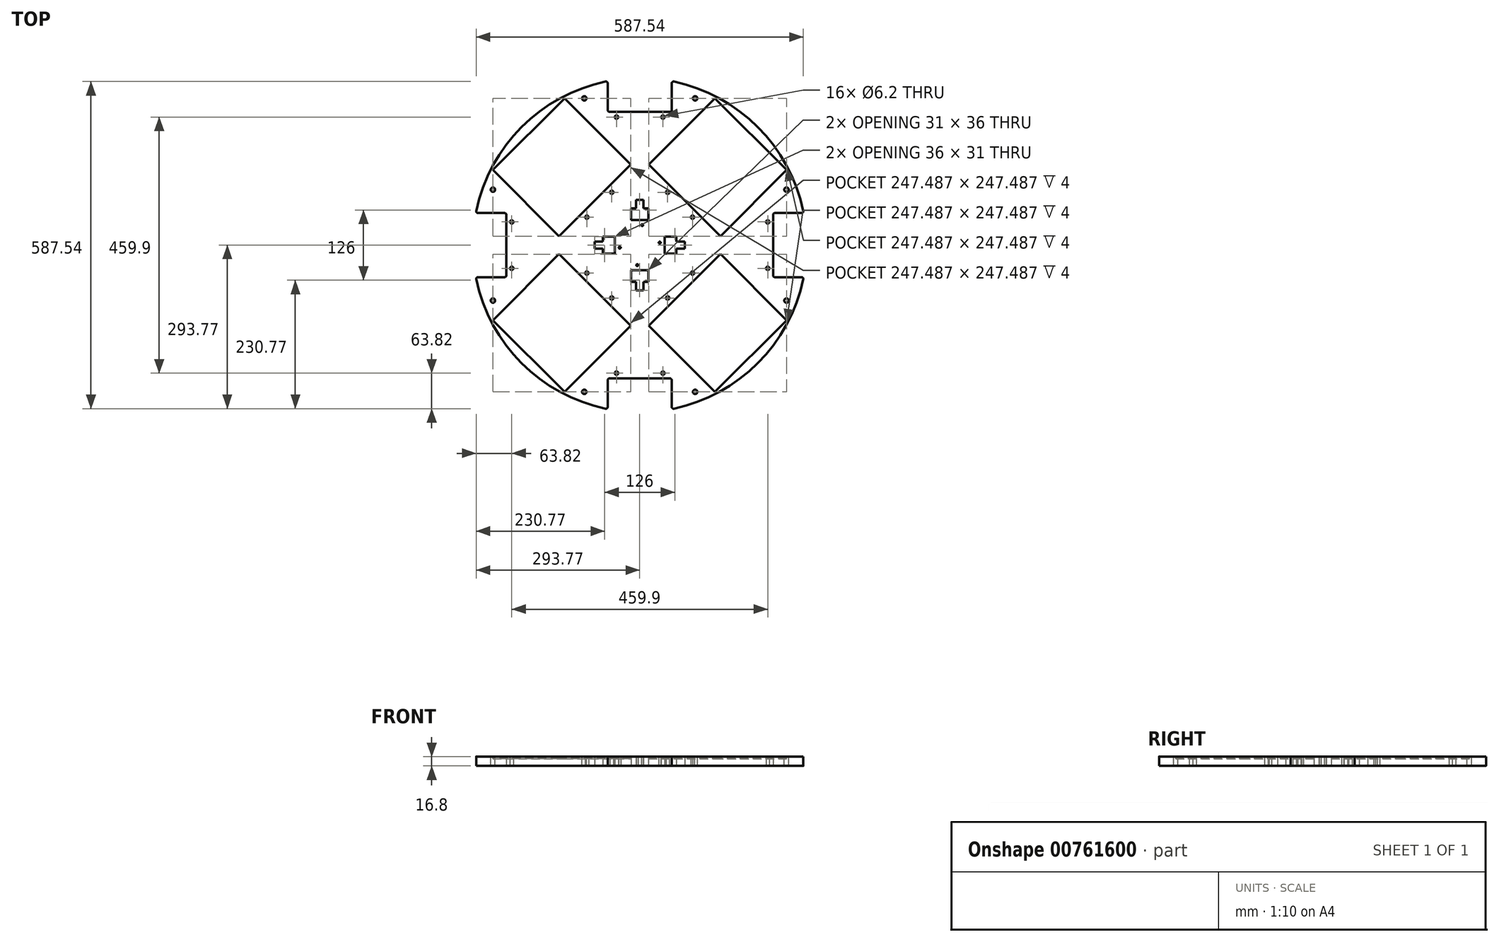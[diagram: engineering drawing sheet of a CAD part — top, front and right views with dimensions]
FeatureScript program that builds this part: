
annotation { "Feature Type Name" : "Feature", "Feature Type Description" : "" }
export const myFeature = defineFeature(function(context is Context, id is Id, definition is map)
    precondition{}
    {
        {
            var Q0;
            Q0=qCreatedBy(makeId("Top.planeOp"),FACE);
            var sketch = newSketch(context, id + "F0", { "sketchPlane" : qUnion([Q0])});
            skCircle(sketch, "E0", {"center": v(0, 0) * mm, "radius": 300 * mm});
            skLineSegment(sketch, "E1", {"start": v(300, 0) * mm, "end": v(-300, 0) * mm, "construction": true});
            skLineSegment(sketch, "E2", {"start": v(0, -300) * mm, "end": v(0, 300) * mm, "construction": true});
            skLineSegment(sketch, "E3.bottom", {"start": v(-296.52, 57.5) * mm, "end": v(-239.5, 57.5) * mm});
            skLineSegment(sketch, "E3.top", {"start": v(-296.52, -57.5) * mm, "end": v(-239.5, -57.5) * mm});
            skLineSegment(sketch, "E3.left", {"start": v(-296.52, 57.5) * mm, "end": v(-296.52, -57.5) * mm, "construction": true});
            skLineSegment(sketch, "E3.right", {"start": v(-239.5, 57.5) * mm, "end": v(-239.5, -57.5) * mm});
            skPoint(sketch, "E3.middle", {"position": v(-268, 0) * mm});
            skLineSegment(sketch, "E4.1.0", {"start": v(-57.5, -296.52) * mm, "end": v(-57.5, -239.5) * mm});
            skLineSegment(sketch, "E4.1.1", {"start": v(57.5, -296.52) * mm, "end": v(57.5, -239.5) * mm});
            skLineSegment(sketch, "E4.1.2", {"start": v(-57.5, -296.52) * mm, "end": v(57.5, -296.52) * mm});
            skLineSegment(sketch, "E4.1.3", {"start": v(-57.5, -239.5) * mm, "end": v(57.5, -239.5) * mm});
            skPoint(sketch, "E4.1.4", {"position": v(0, -268) * mm});
            skLineSegment(sketch, "E4.2.0", {"start": v(296.52, -57.5) * mm, "end": v(239.5, -57.5) * mm});
            skLineSegment(sketch, "E4.2.1", {"start": v(296.52, 57.5) * mm, "end": v(239.5, 57.5) * mm});
            skLineSegment(sketch, "E4.2.2", {"start": v(296.52, -57.5) * mm, "end": v(296.52, 57.5) * mm});
            skLineSegment(sketch, "E4.2.3", {"start": v(239.5, -57.5) * mm, "end": v(239.5, 57.5) * mm});
            skPoint(sketch, "E4.2.4", {"position": v(268, 0) * mm});
            skLineSegment(sketch, "E4.3.0", {"start": v(57.5, 296.52) * mm, "end": v(57.5, 239.5) * mm});
            skLineSegment(sketch, "E4.3.1", {"start": v(-57.5, 296.52) * mm, "end": v(-57.5, 239.5) * mm});
            skLineSegment(sketch, "E4.3.2", {"start": v(57.5, 296.52) * mm, "end": v(-57.5, 296.52) * mm});
            skLineSegment(sketch, "E4.3.3", {"start": v(57.5, 239.5) * mm, "end": v(-57.5, 239.5) * mm});
            skPoint(sketch, "E4.3.4", {"position": v(0, 268) * mm});
            skLineSegment(sketch, "E5", {"start": v(-239.5, -57.5) * mm, "end": v(-94.95, -57.5) * mm, "construction": true});
            skLineSegment(sketch, "E6", {"start": v(-229.95, -41.7) * mm, "end": v(-229.95, 0) * mm, "construction": true});
            skCircle(sketch, "E7", {"center": v(-229.95, -41.7) * mm, "radius": 3.1 * mm});
            skCircle(sketch, "E8.MirrorC", {"center": v(-229.95, 41.7) * mm, "radius": 3.1 * mm});
            skCircle(sketch, "E9.1.0", {"center": v(41.7, -229.95) * mm, "radius": 3.1 * mm});
            skCircle(sketch, "E9.1.1", {"center": v(-41.7, -229.95) * mm, "radius": 3.1 * mm});
            skCircle(sketch, "E9.2.0", {"center": v(229.95, 41.7) * mm, "radius": 3.1 * mm});
            skCircle(sketch, "E9.2.1", {"center": v(229.95, -41.7) * mm, "radius": 3.1 * mm});
            skCircle(sketch, "E9.3.0", {"center": v(-41.7, 229.95) * mm, "radius": 3.1 * mm});
            skCircle(sketch, "E9.3.1", {"center": v(41.7, 229.95) * mm, "radius": 3.1 * mm});
            skLineSegment(sketch, "E10", {"start": v(-94.95, -57.5) * mm, "end": v(-94.95, -50.2) * mm, "construction": true});
            skLineSegment(sketch, "E11", {"start": v(-94.95, -50.2) * mm, "end": v(-239.5, -50.2) * mm, "construction": true});
            skCircle(sketch, "E12", {"center": v(-94.95, -50.2) * mm, "radius": 3.1 * mm});
            skCircle(sketch, "E13.MirrorC", {"center": v(-94.95, 50.2) * mm, "radius": 3.1 * mm});
            skCircle(sketch, "E14.1.0", {"center": v(50.2, -94.95) * mm, "radius": 3.1 * mm});
            skCircle(sketch, "E14.1.1", {"center": v(-50.2, -94.95) * mm, "radius": 3.1 * mm});
            skCircle(sketch, "E14.2.0", {"center": v(94.95, 50.2) * mm, "radius": 3.1 * mm});
            skCircle(sketch, "E14.2.1", {"center": v(94.95, -50.2) * mm, "radius": 3.1 * mm});
            skCircle(sketch, "E14.3.0", {"center": v(-50.2, 94.95) * mm, "radius": 3.1 * mm});
            skCircle(sketch, "E14.3.1", {"center": v(50.2, 94.95) * mm, "radius": 3.1 * mm});
            skLineSegment(sketch, "E15", {"start": v(-294.44, 57.5) * mm, "end": v(-296.52, 57.5) * mm, "construction": true});
            skLineSegment(sketch, "E16", {"start": v(-294.44, 57.5) * mm, "end": v(-294.44, -57.5) * mm, "construction": true});
            skLineSegment(sketch, "E17", {"start": v(-296.52, -57.5) * mm, "end": v(-294.44, -57.5) * mm, "construction": true});
            skLineSegment(sketch, "E18.bottom", {"start": v(-45, -15.5) * mm, "end": v(-66, -15.5) * mm});
            skLineSegment(sketch, "E18.top", {"start": v(-45, 15.5) * mm, "end": v(-66, 15.5) * mm});
            skLineSegment(sketch, "E18.left", {"start": v(-45, -15.5) * mm, "end": v(-45, 15.5) * mm});
            skLineSegment(sketch, "E18.right", {"start": v(-66, -15.5) * mm, "end": v(-66, -6.5) * mm});
            skPoint(sketch, "E18.middle", {"position": v(-55.5, 0) * mm});
            skLineSegment(sketch, "E19", {"start": v(0, 0) * mm, "end": v(-229.45, 229.45) * mm, "construction": true});
            skLineSegment(sketch, "E20.MirrorCS", {"start": v(0, 0) * mm, "end": v(-229.45, -229.45) * mm, "construction": true});
            skLineSegment(sketch, "E21.MirrorCS", {"start": v(0, 0) * mm, "end": v(229.45, -229.45) * mm, "construction": true});
            skLineSegment(sketch, "E22", {"start": v(-66, 6.5) * mm, "end": v(-81, 6.5) * mm});
            skLineSegment(sketch, "E23", {"start": v(-81, 6.5) * mm, "end": v(-81, -6.5) * mm});
            skLineSegment(sketch, "E24", {"start": v(-81, -6.5) * mm, "end": v(-66, -6.5) * mm});
            skPoint(sketch, "E25", {"position": v(-81, 0) * mm});
            skLineSegment(sketch, "E26", {"start": v(-66, 6.5) * mm, "end": v(-66, 15.5) * mm});
            skLineSegment(sketch, "E27", {"start": v(-66, -6.5) * mm, "end": v(-66, 6.5) * mm, "construction": true});
            skLineSegment(sketch, "E28.1.0", {"start": v(-15.5, -45) * mm, "end": v(-15.5, -66) * mm});
            skPoint(sketch, "E28.1.1", {"position": v(0, -81) * mm});
            skLineSegment(sketch, "E28.1.2", {"start": v(-6.5, -66) * mm, "end": v(-6.5, -81) * mm});
            skLineSegment(sketch, "E28.1.3", {"start": v(15.5, -45) * mm, "end": v(15.5, -66) * mm});
            skLineSegment(sketch, "E28.1.4", {"start": v(15.5, -66) * mm, "end": v(6.5, -66) * mm});
            skLineSegment(sketch, "E28.1.5", {"start": v(15.5, -45) * mm, "end": v(-15.5, -45) * mm});
            skLineSegment(sketch, "E28.1.6", {"start": v(6.5, -66) * mm, "end": v(-6.5, -66) * mm, "construction": true});
            skLineSegment(sketch, "E28.1.7", {"start": v(-6.5, -81) * mm, "end": v(6.5, -81) * mm});
            skLineSegment(sketch, "E28.1.8", {"start": v(-6.5, -66) * mm, "end": v(-15.5, -66) * mm});
            skLineSegment(sketch, "E28.1.9", {"start": v(6.5, -81) * mm, "end": v(6.5, -66) * mm});
            skLineSegment(sketch, "E28.2.0", {"start": v(45, -15.5) * mm, "end": v(66, -15.5) * mm});
            skPoint(sketch, "E28.2.1", {"position": v(81, 0) * mm});
            skLineSegment(sketch, "E28.2.2", {"start": v(66, -6.5) * mm, "end": v(81, -6.5) * mm});
            skLineSegment(sketch, "E28.2.3", {"start": v(45, 15.5) * mm, "end": v(66, 15.5) * mm});
            skLineSegment(sketch, "E28.2.4", {"start": v(66, 15.5) * mm, "end": v(66, 6.5) * mm});
            skLineSegment(sketch, "E28.2.5", {"start": v(45, 15.5) * mm, "end": v(45, -15.5) * mm});
            skLineSegment(sketch, "E28.2.6", {"start": v(66, 6.5) * mm, "end": v(66, -6.5) * mm, "construction": true});
            skLineSegment(sketch, "E28.2.7", {"start": v(81, -6.5) * mm, "end": v(81, 6.5) * mm});
            skLineSegment(sketch, "E28.2.8", {"start": v(66, -6.5) * mm, "end": v(66, -15.5) * mm});
            skLineSegment(sketch, "E28.2.9", {"start": v(81, 6.5) * mm, "end": v(66, 6.5) * mm});
            skLineSegment(sketch, "E28.3.0", {"start": v(15.5, 45) * mm, "end": v(15.5, 66) * mm});
            skPoint(sketch, "E28.3.1", {"position": v(0, 81) * mm});
            skLineSegment(sketch, "E28.3.2", {"start": v(6.5, 66) * mm, "end": v(6.5, 81) * mm});
            skLineSegment(sketch, "E28.3.3", {"start": v(-15.5, 45) * mm, "end": v(-15.5, 66) * mm});
            skLineSegment(sketch, "E28.3.4", {"start": v(-15.5, 66) * mm, "end": v(-6.5, 66) * mm});
            skLineSegment(sketch, "E28.3.5", {"start": v(-15.5, 45) * mm, "end": v(15.5, 45) * mm});
            skLineSegment(sketch, "E28.3.6", {"start": v(-6.5, 66) * mm, "end": v(6.5, 66) * mm, "construction": true});
            skLineSegment(sketch, "E28.3.7", {"start": v(6.5, 81) * mm, "end": v(-6.5, 81) * mm});
            skLineSegment(sketch, "E28.3.8", {"start": v(6.5, 66) * mm, "end": v(15.5, 66) * mm});
            skLineSegment(sketch, "E28.3.9", {"start": v(-6.5, 81) * mm, "end": v(-6.5, 66) * mm});
            skLineSegment(sketch, "E29", {"start": v(-23.74, -23.74) * mm, "end": v(-46.55, -0.94) * mm, "construction": true});
            skLineSegment(sketch, "E30", {"start": v(-23.74, -23.74) * mm, "end": v(-0.94, -46.55) * mm, "construction": true});
            skLineSegment(sketch, "E31.MirrorCS", {"start": v(23.74, 23.74) * mm, "end": v(0.94, 46.55) * mm, "construction": true});
            skLineSegment(sketch, "E32.MirrorCS", {"start": v(23.74, 23.74) * mm, "end": v(46.55, 0.94) * mm, "construction": true});
            skLineSegment(sketch, "E33", {"start": v(-46.55, -0.94) * mm, "end": v(0.94, 46.55) * mm, "construction": true});
            skLineSegment(sketch, "E34", {"start": v(-0.94, -46.55) * mm, "end": v(46.55, 0.94) * mm, "construction": true});
            skCircle(sketch, "E35", {"center": v(4.47, 35.94) * mm, "radius": 1.75 * mm});
            skCircle(sketch, "E36.MirrorC", {"center": v(35.94, 4.47) * mm, "radius": 1.75 * mm});
            skCircle(sketch, "E37.MirrorC", {"center": v(-35.94, -4.47) * mm, "radius": 1.75 * mm});
            skCircle(sketch, "E38.MirrorC", {"center": v(-4.47, -35.94) * mm, "radius": 1.75 * mm});
            skLineSegment(sketch, "E39", {"start": v(-35.94, -4.47) * mm, "end": v(-4.47, -35.94) * mm, "construction": true});
            skLineSegment(sketch, "E40", {"start": v(-35.94, -4.47) * mm, "end": v(4.47, 35.94) * mm, "construction": true});
            skSolve(sketch);
        }
        {
            var Q0;
            {var subQ6=sQuery(id+"F0.wireOp",EDGE,"E3.right");Q0=makeQuery(id+"F0.imprint","IMPRINT",FACE,{"disambiguationData":[TD([[makeQuery(id+"F0.imprint","IMPRINT",EDGE,{"derivedFrom":subQ6}),1.0]])]});}
            extrude(context, id + "F1", {"entities" : qUnion([Q0]), "depth" : 16.8 * mm, "offsetDistance" : 25 * mm});
        }
        {
            var Q0;
            Q0=makeQuery(id+"F1.opExtrude","CAP_FACE",FACE,{"disambiguationData":[OSD([sQuery(id+"F0.wireOp",EDGE,"E0"),sQuery(id+"F0.wireOp",EDGE,"E3.bottom"),sQuery(id+"F0.wireOp",EDGE,"E3.top"),sQuery(id+"F0.wireOp",EDGE,"E3.left"),sQuery(id+"F0.wireOp",EDGE,"E3.right"),sQuery(id+"F0.wireOp",EDGE,"E4.1.0"),sQuery(id+"F0.wireOp",EDGE,"E4.1.1"),sQuery(id+"F0.wireOp",EDGE,"E4.1.2"),sQuery(id+"F0.wireOp",EDGE,"E4.1.3"),sQuery(id+"F0.wireOp",EDGE,"E4.2.0"),sQuery(id+"F0.wireOp",EDGE,"E4.2.1"),sQuery(id+"F0.wireOp",EDGE,"E4.2.2"),sQuery(id+"F0.wireOp",EDGE,"E4.2.3"),sQuery(id+"F0.wireOp",EDGE,"E4.3.0"),sQuery(id+"F0.wireOp",EDGE,"E4.3.1"),sQuery(id+"F0.wireOp",EDGE,"E4.3.2"),sQuery(id+"F0.wireOp",EDGE,"E4.3.3"),sQuery(id+"F0.wireOp",EDGE,"E7"),sQuery(id+"F0.wireOp",EDGE,"E8.MirrorC"),sQuery(id+"F0.wireOp",EDGE,"E9.1.0"),sQuery(id+"F0.wireOp",EDGE,"E9.1.1"),sQuery(id+"F0.wireOp",EDGE,"E9.2.0"),sQuery(id+"F0.wireOp",EDGE,"E9.2.1"),sQuery(id+"F0.wireOp",EDGE,"E9.3.0"),sQuery(id+"F0.wireOp",EDGE,"E9.3.1"),sQuery(id+"F0.wireOp",EDGE,"E12"),sQuery(id+"F0.wireOp",EDGE,"E13.MirrorC"),sQuery(id+"F0.wireOp",EDGE,"E14.1.0"),sQuery(id+"F0.wireOp",EDGE,"E14.1.1"),sQuery(id+"F0.wireOp",EDGE,"E14.2.0"),sQuery(id+"F0.wireOp",EDGE,"E14.2.1"),sQuery(id+"F0.wireOp",EDGE,"E14.3.0"),sQuery(id+"F0.wireOp",EDGE,"E14.3.1")])],"isStart":false});
            var sketch = newSketch(context, id + "F2", { "sketchPlane" : qUnion([Q0])});
            skLineSegment(sketch, "E41", {"start": v(0, 0) * mm, "end": v(-212.13, -212.13) * mm, "construction": true});
            skLineSegment(sketch, "E42", {"start": v(0, 0) * mm, "end": v(-300, 0) * mm, "construction": true});
            skLineSegment(sketch, "E43", {"start": v(-263.66, -134.96) * mm, "end": v(-134.96, -263.66) * mm});
            skLineSegment(sketch, "E44", {"start": v(-134.96, -263.66) * mm, "end": v(-16.17, -144.86) * mm});
            skLineSegment(sketch, "E45", {"start": v(-16.17, -144.86) * mm, "end": v(-144.86, -16.17) * mm});
            skLineSegment(sketch, "E46", {"start": v(-144.86, -16.17) * mm, "end": v(-263.66, -134.96) * mm});
            skPoint(sketch, "E47", {"position": v(-199.3, -199.3) * mm});
            skLineSegment(sketch, "E48", {"start": v(0, 0) * mm, "end": v(212.13, 212.13) * mm, "construction": true});
            skLineSegment(sketch, "E49", {"start": v(0, 0) * mm, "end": v(212.13, -212.13) * mm, "construction": true});
            skLineSegment(sketch, "E50", {"start": v(-263.66, -134.96) * mm, "end": v(-266.48, -137.8) * mm});
            skLineSegment(sketch, "E51.1.0", {"start": v(16.17, -144.86) * mm, "end": v(134.96, -263.66) * mm});
            skLineSegment(sketch, "E51.1.1", {"start": v(144.86, -16.17) * mm, "end": v(16.17, -144.86) * mm});
            skLineSegment(sketch, "E51.1.2", {"start": v(263.66, -134.96) * mm, "end": v(144.86, -16.17) * mm});
            skLineSegment(sketch, "E51.1.3", {"start": v(134.96, -263.66) * mm, "end": v(263.66, -134.96) * mm});
            skLineSegment(sketch, "E51.2.0", {"start": v(144.86, 16.17) * mm, "end": v(263.66, 134.96) * mm});
            skLineSegment(sketch, "E51.2.1", {"start": v(16.17, 144.86) * mm, "end": v(144.86, 16.17) * mm});
            skLineSegment(sketch, "E51.2.2", {"start": v(134.96, 263.66) * mm, "end": v(16.17, 144.86) * mm});
            skLineSegment(sketch, "E51.2.3", {"start": v(263.66, 134.96) * mm, "end": v(134.96, 263.66) * mm});
            skLineSegment(sketch, "E51.3.0", {"start": v(-16.17, 144.86) * mm, "end": v(-134.96, 263.66) * mm});
            skLineSegment(sketch, "E51.3.1", {"start": v(-144.86, 16.17) * mm, "end": v(-16.17, 144.86) * mm});
            skLineSegment(sketch, "E51.3.2", {"start": v(-263.66, 134.96) * mm, "end": v(-144.86, 16.17) * mm});
            skLineSegment(sketch, "E51.3.3", {"start": v(-134.96, 263.66) * mm, "end": v(-263.66, 134.96) * mm});
            skPoint(sketch, "E51.center", {"position": v(0, 0) * mm});
            skSolve(sketch);
        }
        {
            var Q0;
            Q0 = qSketchRegion(id + "F2", true);
            extrude(context, id + "F3", {"entities" : qUnion([Q0]), "operationType" : NewBodyOperationType.REMOVE, "oppositeDirection" : true, "depth" : 4 * mm, "offsetDistance" : 25 * mm});
        }
        {
            var Q0;
            Q0=makeQuery(id+"F1.opExtrude","CAP_FACE",FACE,{"disambiguationData":[OSD([sQuery(id+"F0.wireOp",EDGE,"E0"),sQuery(id+"F0.wireOp",EDGE,"E3.bottom"),sQuery(id+"F0.wireOp",EDGE,"E3.top"),sQuery(id+"F0.wireOp",EDGE,"E3.left"),sQuery(id+"F0.wireOp",EDGE,"E3.right"),sQuery(id+"F0.wireOp",EDGE,"E4.1.0"),sQuery(id+"F0.wireOp",EDGE,"E4.1.1"),sQuery(id+"F0.wireOp",EDGE,"E4.1.2"),sQuery(id+"F0.wireOp",EDGE,"E4.1.3"),sQuery(id+"F0.wireOp",EDGE,"E4.2.0"),sQuery(id+"F0.wireOp",EDGE,"E4.2.1"),sQuery(id+"F0.wireOp",EDGE,"E4.2.2"),sQuery(id+"F0.wireOp",EDGE,"E4.2.3"),sQuery(id+"F0.wireOp",EDGE,"E4.3.0"),sQuery(id+"F0.wireOp",EDGE,"E4.3.1"),sQuery(id+"F0.wireOp",EDGE,"E4.3.2"),sQuery(id+"F0.wireOp",EDGE,"E4.3.3"),sQuery(id+"F0.wireOp",EDGE,"E7"),sQuery(id+"F0.wireOp",EDGE,"E8.MirrorC"),sQuery(id+"F0.wireOp",EDGE,"E9.1.0"),sQuery(id+"F0.wireOp",EDGE,"E9.1.1"),sQuery(id+"F0.wireOp",EDGE,"E9.2.0"),sQuery(id+"F0.wireOp",EDGE,"E9.2.1"),sQuery(id+"F0.wireOp",EDGE,"E9.3.0"),sQuery(id+"F0.wireOp",EDGE,"E9.3.1"),sQuery(id+"F0.wireOp",EDGE,"E12"),sQuery(id+"F0.wireOp",EDGE,"E13.MirrorC"),sQuery(id+"F0.wireOp",EDGE,"E14.1.0"),sQuery(id+"F0.wireOp",EDGE,"E14.1.1"),sQuery(id+"F0.wireOp",EDGE,"E14.2.0"),sQuery(id+"F0.wireOp",EDGE,"E14.2.1"),sQuery(id+"F0.wireOp",EDGE,"E14.3.0"),sQuery(id+"F0.wireOp",EDGE,"E14.3.1"),sQuery(id+"F0.wireOp",EDGE,"E18.bottom"),sQuery(id+"F0.wireOp",EDGE,"E18.top"),sQuery(id+"F0.wireOp",EDGE,"E18.left"),sQuery(id+"F0.wireOp",EDGE,"E18.right"),sQuery(id+"F0.wireOp",EDGE,"vhIM6kYj-bil8-T5aC-Hw9W-HzG7wACOchpu.bottom"),sQuery(id+"F0.wireOp",EDGE,"vhIM6kYj-bil8-T5aC-Hw9W-HzG7wACOchpu.top"),sQuery(id+"F0.wireOp",EDGE,"vhIM6kYj-bil8-T5aC-Hw9W-HzG7wACOchpu.left"),sQuery(id+"F0.wireOp",EDGE,"vhIM6kYj-bil8-T5aC-Hw9W-HzG7wACOchpu.right"),sQuery(id+"F0.wireOp",EDGE,"e5db2dc1-b70e-487e-85e1-c1db5f647828.1.0"),sQuery(id+"F0.wireOp",EDGE,"e5db2dc1-b70e-487e-85e1-c1db5f647828.1.1"),sQuery(id+"F0.wireOp",EDGE,"e5db2dc1-b70e-487e-85e1-c1db5f647828.1.2"),sQuery(id+"F0.wireOp",EDGE,"e5db2dc1-b70e-487e-85e1-c1db5f647828.1.3"),sQuery(id+"F0.wireOp",EDGE,"e5db2dc1-b70e-487e-85e1-c1db5f647828.1.4"),sQuery(id+"F0.wireOp",EDGE,"e5db2dc1-b70e-487e-85e1-c1db5f647828.1.5"),sQuery(id+"F0.wireOp",EDGE,"e5db2dc1-b70e-487e-85e1-c1db5f647828.1.6"),sQuery(id+"F0.wireOp",EDGE,"e5db2dc1-b70e-487e-85e1-c1db5f647828.1.7"),sQuery(id+"F0.wireOp",EDGE,"e5db2dc1-b70e-487e-85e1-c1db5f647828.2.0"),sQuery(id+"F0.wireOp",EDGE,"e5db2dc1-b70e-487e-85e1-c1db5f647828.2.1"),sQuery(id+"F0.wireOp",EDGE,"e5db2dc1-b70e-487e-85e1-c1db5f647828.2.2"),sQuery(id+"F0.wireOp",EDGE,"e5db2dc1-b70e-487e-85e1-c1db5f647828.2.3"),sQuery(id+"F0.wireOp",EDGE,"e5db2dc1-b70e-487e-85e1-c1db5f647828.2.4"),sQuery(id+"F0.wireOp",EDGE,"e5db2dc1-b70e-487e-85e1-c1db5f647828.2.5"),sQuery(id+"F0.wireOp",EDGE,"e5db2dc1-b70e-487e-85e1-c1db5f647828.2.6"),sQuery(id+"F0.wireOp",EDGE,"e5db2dc1-b70e-487e-85e1-c1db5f647828.2.7"),sQuery(id+"F0.wireOp",EDGE,"e5db2dc1-b70e-487e-85e1-c1db5f647828.3.0"),sQuery(id+"F0.wireOp",EDGE,"e5db2dc1-b70e-487e-85e1-c1db5f647828.3.1"),sQuery(id+"F0.wireOp",EDGE,"e5db2dc1-b70e-487e-85e1-c1db5f647828.3.2"),sQuery(id+"F0.wireOp",EDGE,"e5db2dc1-b70e-487e-85e1-c1db5f647828.3.3"),sQuery(id+"F0.wireOp",EDGE,"e5db2dc1-b70e-487e-85e1-c1db5f647828.3.4"),sQuery(id+"F0.wireOp",EDGE,"e5db2dc1-b70e-487e-85e1-c1db5f647828.3.5"),sQuery(id+"F0.wireOp",EDGE,"e5db2dc1-b70e-487e-85e1-c1db5f647828.3.6"),sQuery(id+"F0.wireOp",EDGE,"e5db2dc1-b70e-487e-85e1-c1db5f647828.3.7")])],"isStart":false});
            var sketch = newSketch(context, id + "F4", { "sketchPlane" : qUnion([Q0])});
            skLineSegment(sketch, "E52", {"start": v(-263.66, -99.6) * mm, "end": v(-245.98, -117.28) * mm, "construction": true});
            skCircle(sketch, "E53", {"center": v(-263.66, -99.6) * mm, "radius": 4 * mm});
            skLineSegment(sketch, "E54", {"start": v(-99.6, -263.66) * mm, "end": v(-117.28, -245.98) * mm, "construction": true});
            skCircle(sketch, "E55", {"center": v(-99.6, -263.66) * mm, "radius": 4 * mm});
            skCircle(sketch, "E56.1.0", {"center": v(99.6, -263.66) * mm, "radius": 4 * mm});
            skCircle(sketch, "E56.1.1", {"center": v(263.66, -99.6) * mm, "radius": 4 * mm});
            skCircle(sketch, "E56.2.0", {"center": v(263.66, 99.6) * mm, "radius": 4 * mm});
            skCircle(sketch, "E56.2.1", {"center": v(99.6, 263.66) * mm, "radius": 4 * mm});
            skCircle(sketch, "E56.3.0", {"center": v(-99.6, 263.66) * mm, "radius": 4 * mm});
            skCircle(sketch, "E56.3.1", {"center": v(-263.66, 99.6) * mm, "radius": 4 * mm});
            skPoint(sketch, "E56.center", {"position": v(0, 0) * mm});
            skSolve(sketch);
        }
        {
            var Q0;
            Q0 = qSketchRegion(id + "F4", true);
            extrude(context, id + "F5", {"entities" : qUnion([Q0]), "operationType" : NewBodyOperationType.REMOVE, "oppositeDirection" : true, "depth" : 25 * mm, "offsetDistance" : 25 * mm});
        }
        {
            var Q0;
            Q0=makeQuery(id+"F1.opExtrude","SWEPT_EDGE",EDGE,{"disambiguationData":[OSD([sQuery(id+"F0.wireOp",EDGE,"E4.1.1"),sQuery(id+"F0.wireOp",EDGE,"E4.1.3")])]});
            var Q1;
            Q1=makeQuery(id+"F1.opExtrude","SWEPT_EDGE",EDGE,{"disambiguationData":[OSD([sQuery(id+"F0.wireOp",EDGE,"E0"),sQuery(id+"F0.wireOp",EDGE,"E4.1.1")])]});
            var Q2;
            Q2=makeQuery(id+"F1.opExtrude","SWEPT_EDGE",EDGE,{"disambiguationData":[OSD([sQuery(id+"F0.wireOp",EDGE,"E4.1.0"),sQuery(id+"F0.wireOp",EDGE,"E4.1.3")])]});
            var Q3;
            Q3=makeQuery(id+"F1.opExtrude","SWEPT_EDGE",EDGE,{"disambiguationData":[OSD([sQuery(id+"F0.wireOp",EDGE,"E0"),sQuery(id+"F0.wireOp",EDGE,"E4.1.0")])]});
            var Q4;
            Q4=makeQuery(id+"F1.opExtrude","SWEPT_EDGE",EDGE,{"disambiguationData":[OSD([sQuery(id+"F0.wireOp",EDGE,"E0"),sQuery(id+"F0.wireOp",EDGE,"E3.bottom")])]});
            var Q5;
            Q5=makeQuery(id+"F1.opExtrude","SWEPT_EDGE",EDGE,{"disambiguationData":[OSD([sQuery(id+"F0.wireOp",EDGE,"E3.bottom"),sQuery(id+"F0.wireOp",EDGE,"E3.right")])]});
            var Q6;
            Q6=makeQuery(id+"F1.opExtrude","SWEPT_EDGE",EDGE,{"disambiguationData":[OSD([sQuery(id+"F0.wireOp",EDGE,"E3.top"),sQuery(id+"F0.wireOp",EDGE,"E3.right")])]});
            var Q7;
            Q7=makeQuery(id+"F1.opExtrude","SWEPT_EDGE",EDGE,{"disambiguationData":[OSD([sQuery(id+"F0.wireOp",EDGE,"E0"),sQuery(id+"F0.wireOp",EDGE,"E3.top")])]});
            var Q8;
            Q8=makeQuery(id+"F1.opExtrude","SWEPT_EDGE",EDGE,{"disambiguationData":[OSD([sQuery(id+"F0.wireOp",EDGE,"E4.3.0"),sQuery(id+"F0.wireOp",EDGE,"E4.3.3")])]});
            var Q9;
            Q9=makeQuery(id+"F1.opExtrude","SWEPT_EDGE",EDGE,{"disambiguationData":[OSD([sQuery(id+"F0.wireOp",EDGE,"E0"),sQuery(id+"F0.wireOp",EDGE,"E4.2.0")])]});
            var Q10;
            Q10=makeQuery(id+"F1.opExtrude","SWEPT_EDGE",EDGE,{"disambiguationData":[OSD([sQuery(id+"F0.wireOp",EDGE,"E0"),sQuery(id+"F0.wireOp",EDGE,"E4.3.0")])]});
            var Q11;
            Q11=makeQuery(id+"F1.opExtrude","SWEPT_EDGE",EDGE,{"disambiguationData":[OSD([sQuery(id+"F0.wireOp",EDGE,"E4.3.1"),sQuery(id+"F0.wireOp",EDGE,"E4.3.3")])]});
            var Q12;
            Q12=makeQuery(id+"F1.opExtrude","SWEPT_EDGE",EDGE,{"disambiguationData":[OSD([sQuery(id+"F0.wireOp",EDGE,"E0"),sQuery(id+"F0.wireOp",EDGE,"E4.3.1")])]});
            var Q13;
            Q13=makeQuery(id+"F1.opExtrude","SWEPT_EDGE",EDGE,{"disambiguationData":[OSD([sQuery(id+"F0.wireOp",EDGE,"E4.2.0"),sQuery(id+"F0.wireOp",EDGE,"E4.2.3")])]});
            var Q14;
            Q14=makeQuery(id+"F1.opExtrude","SWEPT_EDGE",EDGE,{"disambiguationData":[OSD([sQuery(id+"F0.wireOp",EDGE,"E4.2.1"),sQuery(id+"F0.wireOp",EDGE,"E4.2.3")])]});
            var Q15;
            Q15=makeQuery(id+"F1.opExtrude","SWEPT_EDGE",EDGE,{"disambiguationData":[OSD([sQuery(id+"F0.wireOp",EDGE,"E0"),sQuery(id+"F0.wireOp",EDGE,"E4.2.1")])]});
            fillet(context, id + "F6", {"entities" : qUnion([Q0, Q1, Q2, Q3, Q4, Q5, Q6, Q7, Q8, Q9, Q10, Q11, Q12, Q13, Q14, Q15]), "radius" : 3 * mm, "tangentPropagation" : true, "allowEdgeOverflow" : false});
        }
    });
